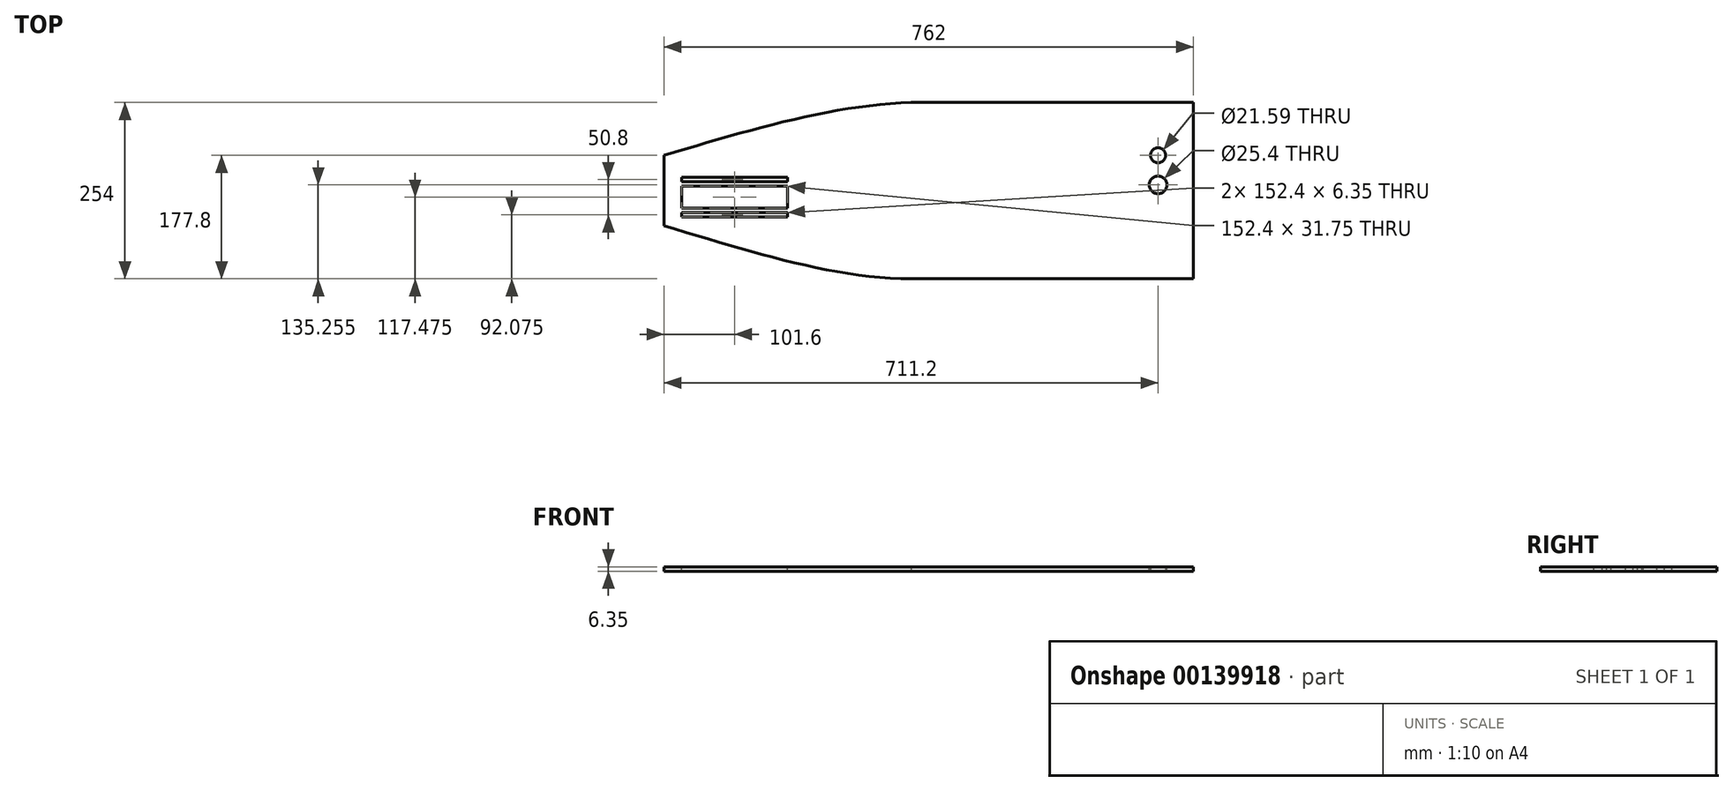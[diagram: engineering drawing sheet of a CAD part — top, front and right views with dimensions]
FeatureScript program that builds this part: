
annotation { "Feature Type Name" : "Feature", "Feature Type Description" : "" }
export const myFeature = defineFeature(function(context is Context, id is Id, definition is map)
    precondition{}
    {
        {
            var Q0;
            Q0=qCreatedBy(makeId("Top.planeOp"),FACE);
            var sketch = newSketch(context, id + "F0", { "sketchPlane" : qUnion([Q0])});
            skLineSegment(sketch, "E0.bottom", {"start": v(0, 0) * mm, "end": v(406.4, 0) * mm});
            skLineSegment(sketch, "E0.top", {"start": v(0, 254) * mm, "end": v(406.4, 254) * mm});
            skLineSegment(sketch, "E0.left", {"start": v(0, 0) * mm, "end": v(0, 254) * mm});
            skLineSegment(sketch, "E0.right", {"start": v(406.4, 0) * mm, "end": v(406.4, 254) * mm});
            skCircle(sketch, "E1", {"center": v(355.6, 177.8) * mm, "radius": 10.8 * mm});
            skSolve(sketch);
        }
        {
            var Q0;
            Q0=makeQuery(id+"F0.imprint","IMPRINT",FACE,{"disambiguationData":[TD([[makeQuery(id+"F0.imprint","IMPRINT",EDGE,{"derivedFrom":sQuery(id+"F0.wireOp",EDGE,"E0.bottom")}),1.0]])]});
            extrude(context, id + "F1", {"entities" : qUnion([Q0]), "depth" : 6.35 * mm});
        }
        {
            var Q0;
            Q0=makeQuery(id+"F1.opExtrude","SWEPT_FACE",FACE,{"disambiguationData":[OSD([sQuery(id+"F0.wireOp",EDGE,"E0.left")])]});
            var sketch = newSketch(context, id + "F2", { "sketchPlane" : qUnion([Q0])});
            skLineSegment(sketch, "E2.bottom", {"start": v(-177.8, 6.35) * mm, "end": v(-76.2, 6.35) * mm});
            skLineSegment(sketch, "E2.top", {"start": v(-177.8, 0) * mm, "end": v(-76.2, 0) * mm});
            skLineSegment(sketch, "E2.left", {"start": v(-177.8, 6.35) * mm, "end": v(-177.8, 0) * mm});
            skLineSegment(sketch, "E2.right", {"start": v(-76.2, 6.35) * mm, "end": v(-76.2, 0) * mm});
            skSolve(sketch);
        }
        {
            var Q0;
            Q0=makeQuery(id+"F2.imprint","IMPRINT",FACE,{"disambiguationData":[TD([[makeQuery(id+"F2.imprint","IMPRINT",EDGE,{"derivedFrom":sQuery(id+"F2.wireOp",EDGE,"E2.bottom")}),1.0]])]});
            extrude(context, id + "F3", {"entities" : qUnion([Q0]), "operationType" : NewBodyOperationType.ADD, "depth" : 355.6 * mm});
        }
        {
            var Q0;
            Q0=makeQuery(id+"F3.boolean.opBoolean","MERGE",FACE,{"derivedFrom":[makeQuery(id+"F1.opExtrude","CAP_FACE",FACE,{"disambiguationData":[OSD([sQuery(id+"F0.wireOp",EDGE,"E0.bottom"),sQuery(id+"F0.wireOp",EDGE,"E0.top"),sQuery(id+"F0.wireOp",EDGE,"E0.left"),sQuery(id+"F0.wireOp",EDGE,"E0.right")])],"isStart":false}),makeQuery(id+"F3.opExtrude","SWEPT_FACE",FACE,{"disambiguationData":[OSD([sQuery(id+"F2.wireOp",EDGE,"E2.bottom")])]})]});
            var sketch = newSketch(context, id + "F4", { "sketchPlane" : qUnion([Q0])});
            skFitSpline(sketch, "E3", {"points": [v(0, 254) * mm, v(-355.6, 177.8) * mm], "startDerivative": vector(-338.69, -10.21) * mm, "endDerivative": vector(-351.04, -104.75) * mm});
            skSolve(sketch);
        }
        {
            var Q0;
            Q0=makeQuery(id+"F4.imprint","IMPRINT",FACE,{"disambiguationData":[TD([[makeQuery(id+"F4.imprint","IMPRINT",EDGE,{"derivedFrom":sQuery(id+"F4.wireOp",EDGE,"E3")}),1.0]])]});
            extrude(context, id + "F5", {"entities" : qUnion([Q0]), "operationType" : NewBodyOperationType.ADD, "oppositeDirection" : true, "depth" : 6.35 * mm});
        }
        {
            var Q0;
            {var subQ0=sQuery(id+"F2.wireOp",EDGE,"E2.bottom");var subQ1=sQuery(id+"F0.wireOp",EDGE,"E0.left");Q0=makeQuery(id+"F5.boolean.opBoolean","MERGE",FACE,{"derivedFrom":[makeQuery(id+"F3.boolean.opBoolean","MERGE",FACE,{"derivedFrom":[makeQuery(id+"F1.opExtrude","CAP_FACE",FACE,{"disambiguationData":[OSD([sQuery(id+"F0.wireOp",EDGE,"E0.bottom"),sQuery(id+"F0.wireOp",EDGE,"E0.top"),subQ1,sQuery(id+"F0.wireOp",EDGE,"E0.right")])],"isStart":false}),makeQuery(id+"F3.opExtrude","SWEPT_FACE",FACE,{"disambiguationData":[OSD([subQ0])]})]}),makeQuery(id+"F5.opExtrude","CAP_FACE",FACE,{"disambiguationData":[OSD([subQ1,subQ0,sQuery(id+"F2.wireOp",EDGE,"E2.left"),sQuery(id+"F4.wireOp",EDGE,"E3")])],"isStart":true})]});}
            var sketch = newSketch(context, id + "F6", { "sketchPlane" : qUnion([Q0])});
            skFitSpline(sketch, "E4", {"points": [v(0, 0) * mm, v(-355.6, 76.2) * mm], "startDerivative": vector(-342.36, 0) * mm, "endDerivative": vector(-356.27, 104.85) * mm});
            skSolve(sketch);
        }
        {
            var Q0;
            Q0=makeQuery(id+"F6.imprint","IMPRINT",FACE,{"disambiguationData":[TD([[makeQuery(id+"F6.imprint","IMPRINT",EDGE,{"derivedFrom":sQuery(id+"F6.wireOp",EDGE,"E4")}),-1.0]])]});
            extrude(context, id + "F7", {"entities" : qUnion([Q0]), "operationType" : NewBodyOperationType.ADD, "oppositeDirection" : true, "depth" : 6.35 * mm});
        }
        {
            var Q0;
            {var subQ0=sQuery(id+"F2.wireOp",EDGE,"E2.bottom");var subQ1=sQuery(id+"F0.wireOp",EDGE,"E0.left");Q0=makeQuery(id+"F7.boolean.opBoolean","MERGE",FACE,{"derivedFrom":[makeQuery(id+"F5.boolean.opBoolean","MERGE",FACE,{"derivedFrom":[makeQuery(id+"F3.boolean.opBoolean","MERGE",FACE,{"derivedFrom":[makeQuery(id+"F1.opExtrude","CAP_FACE",FACE,{"disambiguationData":[OSD([sQuery(id+"F0.wireOp",EDGE,"E0.bottom"),sQuery(id+"F0.wireOp",EDGE,"E0.top"),subQ1,sQuery(id+"F0.wireOp",EDGE,"E0.right")])],"isStart":false}),makeQuery(id+"F3.opExtrude","SWEPT_FACE",FACE,{"disambiguationData":[OSD([subQ0])]})]}),makeQuery(id+"F5.opExtrude","CAP_FACE",FACE,{"disambiguationData":[OSD([subQ1,subQ0,sQuery(id+"F2.wireOp",EDGE,"E2.left"),sQuery(id+"F4.wireOp",EDGE,"E3")])],"isStart":true})]}),makeQuery(id+"F7.opExtrude","CAP_FACE",FACE,{"disambiguationData":[OSD([subQ1,subQ0,sQuery(id+"F2.wireOp",EDGE,"E2.right"),sQuery(id+"F6.wireOp",EDGE,"E4")])],"isStart":true})]});}
            var sketch = newSketch(context, id + "F8", { "sketchPlane" : qUnion([Q0])});
            skLineSegment(sketch, "E5.bottom", {"start": v(-330.2, 133.35) * mm, "end": v(-177.8, 133.35) * mm});
            skLineSegment(sketch, "E5.top", {"start": v(-330.2, 101.6) * mm, "end": v(-177.8, 101.6) * mm});
            skLineSegment(sketch, "E5.left", {"start": v(-330.2, 133.35) * mm, "end": v(-330.2, 101.6) * mm});
            skLineSegment(sketch, "E5.right", {"start": v(-177.8, 133.35) * mm, "end": v(-177.8, 101.6) * mm});
            skSolve(sketch);
        }
        {
            var Q0;
            Q0=makeQuery(id+"F8.imprint","IMPRINT",FACE,{"disambiguationData":[TD([[makeQuery(id+"F8.imprint","IMPRINT",EDGE,{"derivedFrom":sQuery(id+"F8.wireOp",EDGE,"E5.bottom")}),-1.0]])]});
            extrude(context, id + "F9", {"entities" : qUnion([Q0]), "operationType" : NewBodyOperationType.REMOVE, "oppositeDirection" : true, "depth" : 6.35 * mm});
        }
        {
            var Q0;
            {var subQ0=sQuery(id+"F2.wireOp",EDGE,"E2.bottom");var subQ1=sQuery(id+"F0.wireOp",EDGE,"E0.left");Q0=makeQuery(id+"F7.boolean.opBoolean","MERGE",FACE,{"derivedFrom":[makeQuery(id+"F5.boolean.opBoolean","MERGE",FACE,{"derivedFrom":[makeQuery(id+"F3.boolean.opBoolean","MERGE",FACE,{"derivedFrom":[makeQuery(id+"F1.opExtrude","CAP_FACE",FACE,{"disambiguationData":[OSD([sQuery(id+"F0.wireOp",EDGE,"E0.bottom"),sQuery(id+"F0.wireOp",EDGE,"E0.top"),subQ1,sQuery(id+"F0.wireOp",EDGE,"E0.right")])],"isStart":false}),makeQuery(id+"F3.opExtrude","SWEPT_FACE",FACE,{"disambiguationData":[OSD([subQ0])]})]}),makeQuery(id+"F5.opExtrude","CAP_FACE",FACE,{"disambiguationData":[OSD([subQ1,subQ0,sQuery(id+"F2.wireOp",EDGE,"E2.left"),sQuery(id+"F4.wireOp",EDGE,"E3")])],"isStart":true})]}),makeQuery(id+"F7.opExtrude","CAP_FACE",FACE,{"disambiguationData":[OSD([subQ1,subQ0,sQuery(id+"F2.wireOp",EDGE,"E2.right"),sQuery(id+"F6.wireOp",EDGE,"E4")])],"isStart":true})]});}
            var sketch = newSketch(context, id + "F10", { "sketchPlane" : qUnion([Q0])});
            skLineSegment(sketch, "E6.bottom", {"start": v(-330.2, 139.7) * mm, "end": v(-177.8, 139.7) * mm});
            skLineSegment(sketch, "E6.top", {"start": v(-330.2, 146.05) * mm, "end": v(-177.8, 146.05) * mm});
            skLineSegment(sketch, "E6.left", {"start": v(-330.2, 139.7) * mm, "end": v(-330.2, 146.05) * mm});
            skLineSegment(sketch, "E6.right", {"start": v(-177.8, 139.7) * mm, "end": v(-177.8, 146.05) * mm});
            skLineSegment(sketch, "E7", {"start": v(-269.6, 139.7) * mm, "end": v(-269.6, 133.35) * mm});
            skSolve(sketch);
        }
        {
            var Q0;
            Q0=makeQuery(id+"F10.imprint","IMPRINT",FACE,{"disambiguationData":[TD([[makeQuery(id+"F10.imprint","IMPRINT",EDGE,{"derivedFrom":sQuery(id+"F10.wireOp",EDGE,"E6.bottom")}),1.0]])]});
            extrude(context, id + "F11", {"entities" : qUnion([Q0]), "operationType" : NewBodyOperationType.REMOVE, "oppositeDirection" : true, "depth" : 6.35 * mm});
        }
        {
            var Q0;
            {var subQ0=sQuery(id+"F2.wireOp",EDGE,"E2.bottom");var subQ1=sQuery(id+"F0.wireOp",EDGE,"E0.left");Q0=makeQuery(id+"F7.boolean.opBoolean","MERGE",FACE,{"derivedFrom":[makeQuery(id+"F5.boolean.opBoolean","MERGE",FACE,{"derivedFrom":[makeQuery(id+"F3.boolean.opBoolean","MERGE",FACE,{"derivedFrom":[makeQuery(id+"F1.opExtrude","CAP_FACE",FACE,{"disambiguationData":[OSD([sQuery(id+"F0.wireOp",EDGE,"E0.bottom"),sQuery(id+"F0.wireOp",EDGE,"E0.top"),subQ1,sQuery(id+"F0.wireOp",EDGE,"E0.right")])],"isStart":false}),makeQuery(id+"F3.opExtrude","SWEPT_FACE",FACE,{"disambiguationData":[OSD([subQ0])]})]}),makeQuery(id+"F5.opExtrude","CAP_FACE",FACE,{"disambiguationData":[OSD([subQ1,subQ0,sQuery(id+"F2.wireOp",EDGE,"E2.left"),sQuery(id+"F4.wireOp",EDGE,"E3")])],"isStart":true})]}),makeQuery(id+"F7.opExtrude","CAP_FACE",FACE,{"disambiguationData":[OSD([subQ1,subQ0,sQuery(id+"F2.wireOp",EDGE,"E2.right"),sQuery(id+"F6.wireOp",EDGE,"E4")])],"isStart":true})]});}
            var sketch = newSketch(context, id + "F12", { "sketchPlane" : qUnion([Q0])});
            skLineSegment(sketch, "E8.bottom", {"start": v(-330.2, 95.25) * mm, "end": v(-177.8, 95.25) * mm});
            skLineSegment(sketch, "E8.top", {"start": v(-330.2, 88.9) * mm, "end": v(-177.8, 88.9) * mm});
            skLineSegment(sketch, "E8.left", {"start": v(-330.2, 95.25) * mm, "end": v(-330.2, 88.9) * mm});
            skLineSegment(sketch, "E8.right", {"start": v(-177.8, 95.25) * mm, "end": v(-177.8, 88.9) * mm});
            skSolve(sketch);
        }
        {
            var Q0;
            Q0=makeQuery(id+"F12.imprint","IMPRINT",FACE,{"disambiguationData":[TD([[makeQuery(id+"F12.imprint","IMPRINT",EDGE,{"derivedFrom":sQuery(id+"F12.wireOp",EDGE,"E8.bottom")}),-1.0]])]});
            extrude(context, id + "F13", {"entities" : qUnion([Q0]), "operationType" : NewBodyOperationType.REMOVE, "oppositeDirection" : true, "depth" : 6.35 * mm});
        }
        {
            var Q0;
            {var subQ0=sQuery(id+"F2.wireOp",EDGE,"E2.bottom");var subQ1=sQuery(id+"F0.wireOp",EDGE,"E0.left");Q0=makeQuery(id+"F7.boolean.opBoolean","MERGE",FACE,{"derivedFrom":[makeQuery(id+"F5.boolean.opBoolean","MERGE",FACE,{"derivedFrom":[makeQuery(id+"F3.boolean.opBoolean","MERGE",FACE,{"derivedFrom":[makeQuery(id+"F1.opExtrude","CAP_FACE",FACE,{"disambiguationData":[OSD([sQuery(id+"F0.wireOp",EDGE,"E0.bottom"),sQuery(id+"F0.wireOp",EDGE,"E0.top"),subQ1,sQuery(id+"F0.wireOp",EDGE,"E0.right"),sQuery(id+"F0.wireOp",EDGE,"E1")])],"isStart":false}),makeQuery(id+"F3.opExtrude","SWEPT_FACE",FACE,{"disambiguationData":[OSD([subQ0])]})]}),makeQuery(id+"F5.opExtrude","CAP_FACE",FACE,{"disambiguationData":[OSD([subQ1,subQ0,sQuery(id+"F2.wireOp",EDGE,"E2.left"),sQuery(id+"F4.wireOp",EDGE,"E3")])],"isStart":true})]}),makeQuery(id+"F7.opExtrude","CAP_FACE",FACE,{"disambiguationData":[OSD([subQ1,subQ0,sQuery(id+"F2.wireOp",EDGE,"E2.right"),sQuery(id+"F6.wireOp",EDGE,"E4")])],"isStart":true})]});}
            var sketch = newSketch(context, id + "F14", { "sketchPlane" : qUnion([Q0])});
            skLineSegment(sketch, "E9", {"start": v(355.6, 177.8) * mm, "end": v(355.6, 135.26) * mm});
            skCircle(sketch, "E10", {"center": v(355.6, 135.26) * mm, "radius": 12.7 * mm});
            skSolve(sketch);
        }
        {
            var Q0;
            Q0=makeQuery(id+"F14.imprint","IMPRINT",FACE,{"disambiguationData":[TD([[makeQuery(id+"F14.imprint","IMPRINT",EDGE,{"derivedFrom":sQuery(id+"F14.wireOp",EDGE,"E10")}),1.0]])]});
            extrude(context, id + "F15", {"entities" : qUnion([Q0]), "operationType" : NewBodyOperationType.REMOVE, "oppositeDirection" : true, "depth" : 6.35 * mm});
        }
    });
